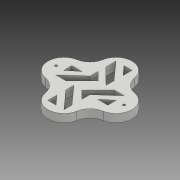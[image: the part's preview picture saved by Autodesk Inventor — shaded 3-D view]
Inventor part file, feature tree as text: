
AUTODESK INVENTOR PART (.ipt)
format: ipt  version: 2018 (Build 220112000, 112)  size: 198,144 bytes
history: native  units: mm
features: extrude x3, sketch x3, fillet x2, other x1
ambient origin geometry x8: Origin, YZ Plane, XZ Plane, XY Plane, X Axis, Y Axis, Z Axis, Center Point
bodies: Body1 (feature_tree)
feature tree (9):
  other  "Sólido1"
  extrude  "Extrusión1"  Depth=10.0mm
  extrude  "Extrusión2"  Depth=85.0mm
  extrude  "Extrusión3"  Depth=20.0mm
  fillet  "Empalme1"  Radius=20.0mm
  fillet  "Empalme2"  Radius=32.5mm
  sketch  "Boceto1"  dims[d0=3.0mm d1=10.0mm]
  sketch  "Boceto2"  dims[d2=20.0mm d3=85.0mm]
  sketch  "Boceto3"  dims[d4=3.0mm d5=20.0mm d6=20.0mm d7=32.5mm d8=20.0mm d9=20.0mm d10=10.0mm d11=32.5mm d12=40.0mm d13=10.0mm d14=0.0mm d15=8.0mm d16=8.0mm d17=5.0mm d18=0.0mm d19=10.0mm d20=10.0mm d21=10.0mm d22=20.0mm d23=6.0mm d24=6.0mm d25=10.0mm d26=10.0mm d27=10.0mm d28=0.0mm d29=20.0mm d30=20.0mm]
